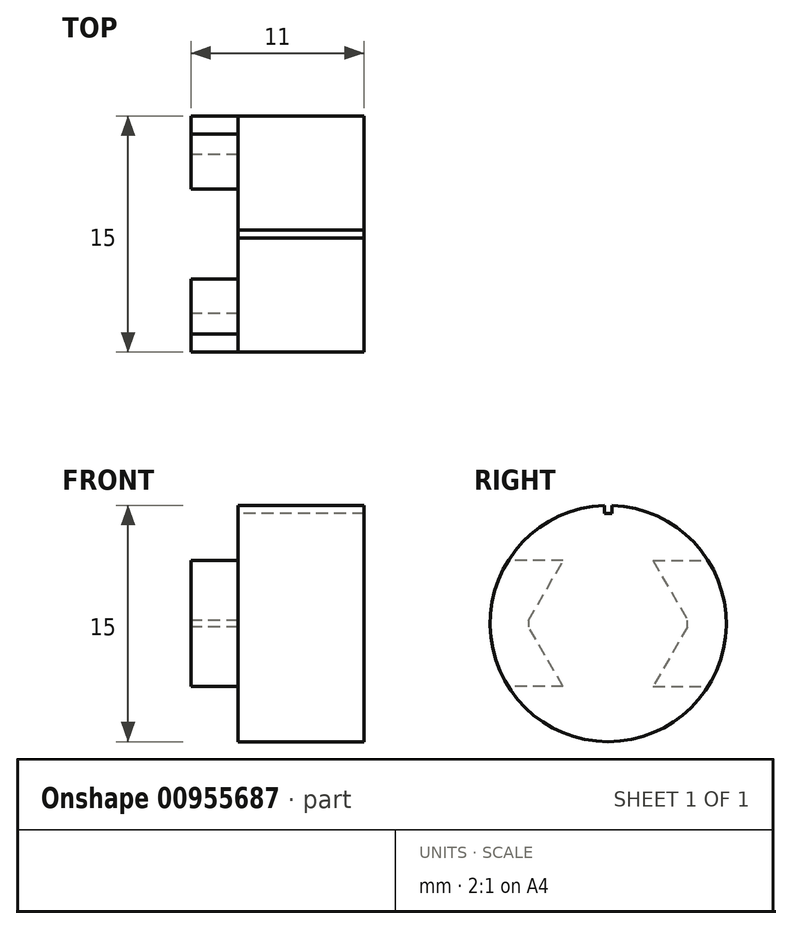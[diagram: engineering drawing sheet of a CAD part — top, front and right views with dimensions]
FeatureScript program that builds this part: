
annotation { "Feature Type Name" : "Feature", "Feature Type Description" : "" }
export const myFeature = defineFeature(function(context is Context, id is Id, definition is map)
    precondition{}
    {
        {
            var Q0;
            Q0=qCreatedBy(makeId("Right.planeOp"),FACE);
            var sketch = newSketch(context, id + "F0", { "sketchPlane" : qUnion([Q0])});
            skLineSegment(sketch, "E0.0", {"start": v(-5.05, 0.21) * mm, "end": v(-2.86, 4) * mm});
            skLineSegment(sketch, "E0.2", {"start": v(2.86, 4) * mm, "end": v(5.05, 0.21) * mm});
            skLineSegment(sketch, "E0.3", {"start": v(5.05, -0.21) * mm, "end": v(2.86, -4) * mm});
            skLineSegment(sketch, "E0.5", {"start": v(-2.86, -4) * mm, "end": v(-5.05, -0.21) * mm});
            skArc(sketch, "E1", {"start": v(-5.05, 0.21) * mm, "mid": v(-5.05, 0) * mm, "end": v(-5.05, -0.21) * mm});
            skPoint(sketch, "E2.orphan", {"position": v(-5.17, 0) * mm});
            skArc(sketch, "E3.trimOffspring", {"start": v(5.05, -0.21) * mm, "mid": v(5.05, 0) * mm, "end": v(5.05, 0.21) * mm});
            skPoint(sketch, "E4.orphan", {"position": v(5.17, 0) * mm});
            skArc(sketch, "E5", {"start": v(-6.34, 4) * mm, "mid": v(-7.5, 0) * mm, "end": v(-6.34, -4) * mm});
            skLineSegment(sketch, "E6", {"start": v(2.86, 4) * mm, "end": v(6.34, 4) * mm});
            skLineSegment(sketch, "E7", {"start": v(-2.86, 4) * mm, "end": v(-6.34, 4) * mm});
            skLineSegment(sketch, "E8", {"start": v(2.86, -4) * mm, "end": v(6.34, -4) * mm});
            skLineSegment(sketch, "E9", {"start": v(-2.86, -4) * mm, "end": v(-6.34, -4) * mm});
            skArc(sketch, "E10.trimOffspring", {"start": v(6.34, -4) * mm, "mid": v(7.5, 0) * mm, "end": v(6.34, 4) * mm});
            skSolve(sketch);
        }
        {
            var Q0;
            Q0=makeQuery(id+"F0.imprint","IMPRINT",FACE,{"disambiguationData":[TD([[makeQuery(id+"F0.imprint","IMPRINT",EDGE,{"derivedFrom":sQuery(id+"F0.wireOp",EDGE,"E0.0")}),1.0]])]});
            var Q1;
            Q1=makeQuery(id+"F0.imprint","IMPRINT",FACE,{"disambiguationData":[TD([[makeQuery(id+"F0.imprint","IMPRINT",EDGE,{"derivedFrom":sQuery(id+"F0.wireOp",EDGE,"E0.2")}),1.0]])]});
            extrude(context, id + "F1", {"entities" : qUnion([Q0, Q1]), "depth" : 3 * mm, "offsetDistance" : 25 * mm});
        }
        {
            var Q0;
            Q0=makeQuery(id+"F1.opExtrude","CAP_FACE",FACE,{"disambiguationData":[OSD([sQuery(id+"F0.wireOp",EDGE,"E0.0"),sQuery(id+"F0.wireOp",EDGE,"E0.5"),sQuery(id+"F0.wireOp",EDGE,"E1"),sQuery(id+"F0.wireOp",EDGE,"E5"),sQuery(id+"F0.wireOp",EDGE,"E7"),sQuery(id+"F0.wireOp",EDGE,"E9")])],"isStart":false});
            var sketch = newSketch(context, id + "F2", { "sketchPlane" : qUnion([Q0])});
            skCircle(sketch, "E11", {"center": v(0, 0) * mm, "radius": 7.5 * mm});
            skSolve(sketch);
        }
        {
            var Q0;
            Q0=makeQuery(id+"F2.imprint","IMPRINT",FACE,{"disambiguationData":[TD([[makeQuery(id+"F2.imprint","IMPRINT",EDGE,{"derivedFrom":makeQuery(id+"F1.opExtrude","CAP_EDGE",EDGE,{"disambiguationData":[OSD([sQuery(id+"F0.wireOp",EDGE,"E0.0")])],"isStart":false})}),1.0]])]});
            var Q1;
            Q1=makeQuery(id+"F2.imprint","IMPRINT",FACE,{"disambiguationData":[TD([[makeQuery(id+"F2.imprint","IMPRINT",EDGE,{"derivedFrom":makeQuery(id+"F1.opExtrude","CAP_EDGE",EDGE,{"disambiguationData":[OSD([sQuery(id+"F0.wireOp",EDGE,"E0.0")])],"isStart":false})}),-1.0]])]});
            extrude(context, id + "F3", {"entities" : qUnion([Q0, Q1]), "depth" : 8 * mm, "offsetDistance" : 25 * mm});
        }
        {
            var Q0;
            Q0=makeQuery(id+"F3.opExtrude","CAP_FACE",FACE,{"disambiguationData":[OSD([sQuery(id+"F2.wireOp",EDGE,"E11")])],"isStart":true});
            var sketch = newSketch(context, id + "F4", { "sketchPlane" : qUnion([Q0])});
            skLineSegment(sketch, "E12.bottom", {"start": v(-0.25, 7.5) * mm, "end": v(0.25, 7.5) * mm});
            skLineSegment(sketch, "E12.top", {"start": v(-0.25, 7) * mm, "end": v(0.25, 7) * mm});
            skLineSegment(sketch, "E12.left", {"start": v(-0.25, 7.5) * mm, "end": v(-0.25, 7) * mm});
            skLineSegment(sketch, "E12.right", {"start": v(0.25, 7.5) * mm, "end": v(0.25, 7) * mm});
            skSolve(sketch);
        }
        {
            var Q0;
            Q0 = qSketchRegion(id + "F4", true);
            extrude(context, id + "F5", {"entities" : qUnion([Q0]), "operationType" : NewBodyOperationType.REMOVE, "oppositeDirection" : true, "depth" : 25 * mm, "offsetDistance" : 25 * mm});
        }
    });
